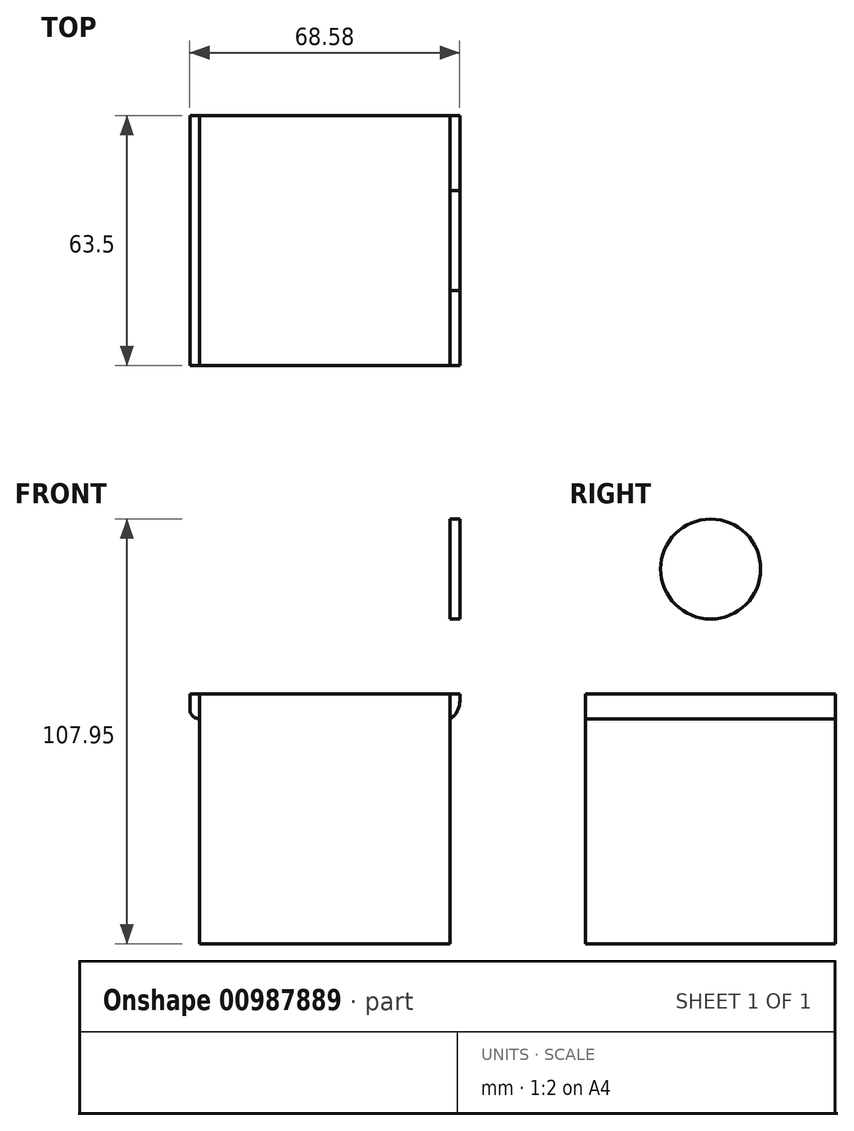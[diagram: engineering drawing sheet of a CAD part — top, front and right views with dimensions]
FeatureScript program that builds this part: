
annotation { "Feature Type Name" : "Feature", "Feature Type Description" : "" }
export const myFeature = defineFeature(function(context is Context, id is Id, definition is map)
    precondition{}
    {
        {
            var Q0;
            Q0=qCreatedBy(makeId("Top.planeOp"),FACE);
            var sketch = newSketch(context, id + "F0", { "sketchPlane" : qUnion([Q0])});
            skLineSegment(sketch, "E0.bottom", {"start": v(-78.16, 69.86) * mm, "end": v(-14.66, 69.86) * mm});
            skLineSegment(sketch, "E0.top", {"start": v(-78.16, 6.36) * mm, "end": v(-14.66, 6.36) * mm});
            skLineSegment(sketch, "E0.left", {"start": v(-78.16, 69.86) * mm, "end": v(-78.16, 6.36) * mm});
            skLineSegment(sketch, "E0.right", {"start": v(-14.66, 69.86) * mm, "end": v(-14.66, 6.36) * mm});
            skSolve(sketch);
        }
        {
            var Q0;
            Q0=makeQuery(id+"F0.imprint","IMPRINT",FACE,{"disambiguationData":[TD([[makeQuery(id+"F0.imprint","IMPRINT",EDGE,{"derivedFrom":sQuery(id+"F0.wireOp",EDGE,"E0.bottom")}),-1.0]])]});
            extrude(context, id + "F1", {"entities" : qUnion([Q0]), "depth" : 127 * mm, "offsetDistance" : 25.4 * mm});
        }
        {
            var Q0;
            Q0=makeQuery(id+"F1.opExtrude","SWEPT_FACE",FACE,{"disambiguationData":[OSD([sQuery(id+"F0.wireOp",EDGE,"E0.bottom")])]});
            var sketch = newSketch(context, id + "F2", { "sketchPlane" : qUnion([Q0])});
            skLineSegment(sketch, "E1.bottom", {"start": v(14.66, 127) * mm, "end": v(78.16, 127) * mm});
            skLineSegment(sketch, "E1.top", {"start": v(14.66, 63.5) * mm, "end": v(78.16, 63.5) * mm});
            skLineSegment(sketch, "E1.left", {"start": v(14.66, 127) * mm, "end": v(14.66, 63.5) * mm});
            skLineSegment(sketch, "E1.right", {"start": v(78.16, 127) * mm, "end": v(78.16, 63.5) * mm});
            skSolve(sketch);
        }
        {
            var Q0;
            Q0=makeQuery(id+"F2.imprint","IMPRINT",FACE,{"disambiguationData":[TD([[makeQuery(id+"F2.imprint","IMPRINT",EDGE,{"derivedFrom":sQuery(id+"F2.wireOp",EDGE,"E1.bottom")}),1.0]])]});
            extrude(context, id + "F3", {"entities" : qUnion([Q0]), "operationType" : NewBodyOperationType.ADD, "depth" : 2.54 * mm, "offsetDistance" : 25.4 * mm});
        }
        {
            var Q0;
            Q0=makeQuery(id+"F3.boolean.opBoolean","MERGE",FACE,{"derivedFrom":[makeQuery(id+"F1.opExtrude","SWEPT_FACE",FACE,{"disambiguationData":[OSD([sQuery(id+"F0.wireOp",EDGE,"E0.left")])]}),makeQuery(id+"F3.opExtrude","SWEPT_FACE",FACE,{"disambiguationData":[OSD([sQuery(id+"F2.wireOp",EDGE,"E1.right")])]})]});
            var sketch = newSketch(context, id + "F4", { "sketchPlane" : qUnion([Q0])});
            skLineSegment(sketch, "E2.bottom", {"start": v(-72.4, 127) * mm, "end": v(10.97, 127) * mm});
            skLineSegment(sketch, "E2.top", {"start": v(-72.4, 63.5) * mm, "end": v(10.97, 63.5) * mm});
            skLineSegment(sketch, "E2.left", {"start": v(-72.4, 127) * mm, "end": v(-72.4, 63.5) * mm});
            skLineSegment(sketch, "E2.right", {"start": v(10.97, 127) * mm, "end": v(10.97, 63.5) * mm});
            skSolve(sketch);
        }
        {
            var Q0;
            {var subQ0=sQuery(id+"F4.wireOp",EDGE,"E2.left");Q0=makeQuery(id+"F4.imprint","IMPRINT",FACE,{"disambiguationData":[TD([[makeQuery(id+"F4.imprint","IMPRINT",EDGE,{"derivedFrom":subQ0}),1.0]])]});}
            extrude(context, id + "F5", {"entities" : qUnion([Q0]), "operationType" : NewBodyOperationType.ADD, "depth" : 2.54 * mm, "offsetDistance" : 25.4 * mm});
        }
        {
            var Q0;
            Q0=makeQuery(id+"F3.boolean.opBoolean","MERGE",FACE,{"derivedFrom":[makeQuery(id+"F1.opExtrude","SWEPT_FACE",FACE,{"disambiguationData":[OSD([sQuery(id+"F0.wireOp",EDGE,"E0.right")])]}),makeQuery(id+"F3.opExtrude","SWEPT_FACE",FACE,{"disambiguationData":[OSD([sQuery(id+"F2.wireOp",EDGE,"E1.left")])]})]});
            var sketch = newSketch(context, id + "F6", { "sketchPlane" : qUnion([Q0])});
            skLineSegment(sketch, "E3.bottom", {"start": v(6.36, 127) * mm, "end": v(72.4, 127) * mm});
            skLineSegment(sketch, "E3.top", {"start": v(6.36, 63.5) * mm, "end": v(72.4, 63.5) * mm});
            skLineSegment(sketch, "E3.left", {"start": v(6.36, 127) * mm, "end": v(6.36, 63.5) * mm});
            skLineSegment(sketch, "E3.right", {"start": v(72.4, 127) * mm, "end": v(72.4, 63.5) * mm});
            skSolve(sketch);
        }
        {
            var Q0;
            Q0=makeQuery(id+"F6.imprint","IMPRINT",FACE,{"disambiguationData":[TD([[makeQuery(id+"F6.imprint","IMPRINT",EDGE,{"derivedFrom":sQuery(id+"F6.wireOp",EDGE,"E3.bottom")}),1.0]])]});
            extrude(context, id + "F7", {"entities" : qUnion([Q0]), "operationType" : NewBodyOperationType.ADD, "depth" : 2.54 * mm, "offsetDistance" : 25.4 * mm});
        }
        {
            var Q0;
            Q0=makeQuery(id+"F7.boolean.opBoolean","MERGE",FACE,{"derivedFrom":[makeQuery(id+"F5.boolean.opBoolean","MERGE",FACE,{"derivedFrom":[makeQuery(id+"F3.opExtrude","CAP_FACE",FACE,{"disambiguationData":[OSD([sQuery(id+"F2.wireOp",EDGE,"E1.bottom"),sQuery(id+"F2.wireOp",EDGE,"E1.top"),sQuery(id+"F2.wireOp",EDGE,"E1.left"),sQuery(id+"F2.wireOp",EDGE,"E1.right")])],"isStart":false}),makeQuery(id+"F5.opExtrude","SWEPT_FACE",FACE,{"disambiguationData":[OSD([sQuery(id+"F4.wireOp",EDGE,"E2.left")])]})]}),makeQuery(id+"F7.opExtrude","SWEPT_FACE",FACE,{"disambiguationData":[OSD([sQuery(id+"F6.wireOp",EDGE,"E3.right")])]})]});
            var sketch = newSketch(context, id + "F8", { "sketchPlane" : qUnion([Q0])});
            skLineSegment(sketch, "E4.bottom", {"start": v(12.12, 127) * mm, "end": v(80.7, 127) * mm});
            skLineSegment(sketch, "E4.top", {"start": v(12.12, 63.5) * mm, "end": v(80.7, 63.5) * mm});
            skLineSegment(sketch, "E4.left", {"start": v(12.12, 127) * mm, "end": v(12.12, 63.5) * mm});
            skLineSegment(sketch, "E4.right", {"start": v(80.7, 127) * mm, "end": v(80.7, 63.5) * mm});
            skSolve(sketch);
        }
        {
            var Q0;
            Q0=makeQuery(id+"F8.imprint","IMPRINT",FACE,{"disambiguationData":[TD([[makeQuery(id+"F8.imprint","IMPRINT",EDGE,{"derivedFrom":sQuery(id+"F8.wireOp",EDGE,"E4.bottom")}),1.0]])]});
            extrude(context, id + "F9", {"entities" : qUnion([Q0]), "operationType" : NewBodyOperationType.REMOVE, "oppositeDirection" : true, "depth" : 2.54 * mm, "offsetDistance" : 25.4 * mm});
        }
        {
            var Q0;
            {var subQ0=sQuery(id+"F0.wireOp",EDGE,"E0.top");Q0=makeQuery(id+"F7.boolean.opBoolean","MERGE",FACE,{"derivedFrom":[makeQuery(id+"F5.boolean.opBoolean","MERGE",FACE,{"derivedFrom":[makeQuery(id+"F1.opExtrude","SWEPT_FACE",FACE,{"disambiguationData":[OSD([subQ0])]}),makeQuery(id+"F5.opExtrude","SWEPT_FACE",FACE,{"disambiguationData":[OSD([subQ0,sQuery(id+"F0.wireOp",EDGE,"E0.left")])]})]}),makeQuery(id+"F7.opExtrude","SWEPT_FACE",FACE,{"disambiguationData":[OSD([sQuery(id+"F6.wireOp",EDGE,"E3.left")])]})]});}
            var sketch = newSketch(context, id + "F10", { "sketchPlane" : qUnion([Q0])});
            skLineSegment(sketch, "E5.bottom", {"start": v(-80.7, 127) * mm, "end": v(-12.12, 127) * mm});
            skLineSegment(sketch, "E5.top", {"start": v(-80.7, 63.5) * mm, "end": v(-12.12, 63.5) * mm});
            skLineSegment(sketch, "E5.left", {"start": v(-80.7, 127) * mm, "end": v(-80.7, 63.5) * mm});
            skLineSegment(sketch, "E5.right", {"start": v(-12.12, 127) * mm, "end": v(-12.12, 63.5) * mm});
            skLineSegment(sketch, "E6", {"start": v(-80.7, 127) * mm, "end": v(-78.16, 127) * mm});
            skLineSegment(sketch, "E7", {"start": v(-78.16, 127) * mm, "end": v(-14.66, 127) * mm});
            skLineSegment(sketch, "E8", {"start": v(-14.66, 127) * mm, "end": v(-12.12, 127) * mm});
            skLineSegment(sketch, "E9.top", {"start": v(-78.16, 63.5) * mm, "end": v(-14.66, 63.5) * mm});
            skLineSegment(sketch, "E9.left", {"start": v(-78.16, 127) * mm, "end": v(-78.16, 63.5) * mm});
            skLineSegment(sketch, "E9.right", {"start": v(-14.66, 127) * mm, "end": v(-14.66, 63.5) * mm});
            skSolve(sketch);
        }
        {
            var Q0;
            {var subQ0=sQuery(id+"F10.wireOp",EDGE,"E9.left");Q0=makeQuery(id+"F10.imprint","IMPRINT",FACE,{"disambiguationData":[TD([[makeQuery(id+"F10.imprint","IMPRINT",EDGE,{"derivedFrom":subQ0}),1.0]])]});}
            extrude(context, id + "F11", {"entities" : qUnion([Q0]), "operationType" : NewBodyOperationType.REMOVE, "endBound" : BoundingType.THROUGH_ALL, "oppositeDirection" : true, "depth" : 25.4 * mm, "offsetDistance" : 25.4 * mm});
        }
        {
            var Q0;
            {var subQ0=sQuery(id+"F0.wireOp",EDGE,"E0.left");var subQ2=sQuery(id+"F4.wireOp",EDGE,"E2.top");Q0=makeQuery(id+"F9.boolean.opBoolean","SPLIT",FACE,{"disambiguationData":[TD([makeQuery(id+"F1.opExtrude","SWEPT_FACE",FACE,{"disambiguationData":[OSD([subQ0])]})])],"derivedFrom":makeQuery(id+"F7.boolean.opBoolean","MERGE",FACE,{"derivedFrom":[makeQuery(id+"F5.boolean.opBoolean","MERGE",FACE,{"derivedFrom":[makeQuery(id+"F3.opExtrude","SWEPT_FACE",FACE,{"disambiguationData":[OSD([sQuery(id+"F2.wireOp",EDGE,"E1.top")])]}),makeQuery(id+"F5.opExtrude","SWEPT_FACE",FACE,{"disambiguationData":[OSD([subQ2])]})]}),makeQuery(id+"F7.opExtrude","SWEPT_FACE",FACE,{"disambiguationData":[OSD([sQuery(id+"F6.wireOp",EDGE,"E3.top")])]})]})});}
            var Q1;
            {var subQ2=sQuery(id+"F6.wireOp",EDGE,"E3.top");Q1=makeQuery(id+"F9.boolean.opBoolean","SPLIT",FACE,{"disambiguationData":[TD([makeQuery(id+"F1.opExtrude","SWEPT_FACE",FACE,{"disambiguationData":[OSD([sQuery(id+"F0.wireOp",EDGE,"E0.right")])]})])],"derivedFrom":makeQuery(id+"F7.boolean.opBoolean","MERGE",FACE,{"derivedFrom":[makeQuery(id+"F5.boolean.opBoolean","MERGE",FACE,{"derivedFrom":[makeQuery(id+"F3.opExtrude","SWEPT_FACE",FACE,{"disambiguationData":[OSD([sQuery(id+"F2.wireOp",EDGE,"E1.top")])]}),makeQuery(id+"F5.opExtrude","SWEPT_FACE",FACE,{"disambiguationData":[OSD([sQuery(id+"F4.wireOp",EDGE,"E2.top")])]})]}),makeQuery(id+"F7.opExtrude","SWEPT_FACE",FACE,{"disambiguationData":[OSD([subQ2])]})]})});}
            extrude(context, id + "F12", {"entities" : qUnion([Q0, Q1]), "depth" : 6.35 * mm, "offsetDistance" : 25.4 * mm});
        }
        {
            var Q0;
            Q0=makeQuery(id+"F12.opExtrude","CAP_EDGE",EDGE,{"disambiguationData":[OSD([sQuery(id+"F4.wireOp",EDGE,"E2.top")])],"isStart":false});
            fillet(context, id + "F13", {"entities" : qUnion([Q0]), "radius" : 2.54 * mm, "tangentPropagation" : true, "allowEdgeOverflow" : false});
        }
        {
            var Q0;
            Q0=makeQuery(id+"F12.opExtrude","CAP_EDGE",EDGE,{"disambiguationData":[OSD([sQuery(id+"F6.wireOp",EDGE,"E3.top")])],"isStart":false});
            fillet(context, id + "F14", {"entities" : qUnion([Q0]), "radius" : 5.08 * mm, "tangentPropagation" : true, "allowEdgeOverflow" : false});
        }
        {
            var Q0;
            Q0=makeQuery(id+"F7.opExtrude","CAP_FACE",FACE,{"disambiguationData":[OSD([sQuery(id+"F6.wireOp",EDGE,"E3.bottom"),sQuery(id+"F6.wireOp",EDGE,"E3.top"),sQuery(id+"F6.wireOp",EDGE,"E3.left"),sQuery(id+"F6.wireOp",EDGE,"E3.right")])],"isStart":false});
            var sketch = newSketch(context, id + "F15", { "sketchPlane" : qUnion([Q0])});
            skLineSegment(sketch, "E10", {"start": v(6.36, 127) * mm, "end": v(69.86, 127) * mm});
            skLineSegment(sketch, "E11", {"start": v(69.86, 127) * mm, "end": v(38.11, 127) * mm});
            skLineSegment(sketch, "E12", {"start": v(38.11, 127) * mm, "end": v(38.11, 63.5) * mm});
            skLineSegment(sketch, "E13", {"start": v(38.11, 63.5) * mm, "end": v(38.11, 95.25) * mm});
            skCircle(sketch, "E14", {"center": v(38.11, 95.25) * mm, "radius": 12.7 * mm});
            skSolve(sketch);
        }
        {
            var Q0;
            {var subQ0=sQuery(id+"F15.wireOp",EDGE,"E13");var subQ1=sQuery(id+"F15.wireOp",EDGE,"E12");var subQ2=makeQuery(id+"F15.imprint","INTERSECT",VERTEX,{"derivedFrom":[subQ1,subQ0]});Q0=makeQuery(id+"F15.imprint","IMPRINT",FACE,{"disambiguationData":[TD([[makeQuery(id+"F15.imprint","IMPRINT",EDGE,{"disambiguationData":[TD([[subQ2,1.0]])],"derivedFrom":subQ1}),-1.0]])]});}
            var Q1;
            {var subQ0=sQuery(id+"F15.wireOp",EDGE,"E13");var subQ1=sQuery(id+"F15.wireOp",EDGE,"E12");var subQ2=makeQuery(id+"F15.imprint","INTERSECT",VERTEX,{"derivedFrom":[subQ1,subQ0]});Q1=makeQuery(id+"F15.imprint","IMPRINT",FACE,{"disambiguationData":[TD([[makeQuery(id+"F15.imprint","IMPRINT",EDGE,{"disambiguationData":[TD([[subQ2,1.0]])],"derivedFrom":subQ1}),1.0]])]});}
            extrude(context, id + "F16", {"entities" : qUnion([Q0, Q1]), "operationType" : NewBodyOperationType.REMOVE, "oppositeDirection" : true, "depth" : 127 * mm, "offsetDistance" : 25.4 * mm});
        }
        {
            var Q0;
            Q0=makeQuery(id+"F5.opExtrude","CAP_FACE",FACE,{"disambiguationData":[OSD([sQuery(id+"F0.wireOp",EDGE,"E0.top"),sQuery(id+"F0.wireOp",EDGE,"E0.left"),sQuery(id+"F4.wireOp",EDGE,"E2.bottom"),sQuery(id+"F4.wireOp",EDGE,"E2.top"),sQuery(id+"F4.wireOp",EDGE,"E2.left")])],"isStart":false});
            var sketch = newSketch(context, id + "F17", { "sketchPlane" : qUnion([Q0])});
            skLineSegment(sketch, "E15", {"start": v(-69.86, 127) * mm, "end": v(-38.11, 127) * mm});
            skLineSegment(sketch, "E16", {"start": v(-38.11, 127) * mm, "end": v(-38.11, 63.5) * mm});
            skLineSegment(sketch, "E17", {"start": v(-38.11, 63.5) * mm, "end": v(-38.11, 95.25) * mm});
            skLineSegment(sketch, "E18", {"start": v(-38.11, 95.25) * mm, "end": v(-69.86, 95.25) * mm});
            skCircle(sketch, "E19", {"center": v(-38.11, 95.25) * mm, "radius": 12.7 * mm});
            skSolve(sketch);
        }
        {
            var Q0;
            {var subQ1=sQuery(id+"F17.wireOp",EDGE,"E16");var subQ3=sQuery(id+"F17.wireOp",EDGE,"E19");var subQ4=makeQuery(id+"F17.imprint","INTERSECT",VERTEX,{"derivedFrom":[subQ1,subQ3]});Q0=makeQuery(id+"F17.imprint","IMPRINT",FACE,{"disambiguationData":[TD([[makeQuery(id+"F17.imprint","IMPRINT",EDGE,{"disambiguationData":[TD([[subQ4,-1.0]])],"derivedFrom":subQ3}),1.0]])]});}
            var Q1;
            {var subQ1=sQuery(id+"F17.wireOp",EDGE,"E17");var subQ3=sQuery(id+"F17.wireOp",EDGE,"E19");var subQ4=makeQuery(id+"F17.imprint","INTERSECT",VERTEX,{"derivedFrom":[subQ1,subQ3]});Q1=makeQuery(id+"F17.imprint","IMPRINT",FACE,{"disambiguationData":[TD([[makeQuery(id+"F17.imprint","IMPRINT",EDGE,{"disambiguationData":[TD([[subQ4,1.0]])],"derivedFrom":subQ3}),1.0]])]});}
            var Q2;
            {var subQ1=sQuery(id+"F17.wireOp",EDGE,"E16");var subQ3=sQuery(id+"F17.wireOp",EDGE,"E19");var subQ4=makeQuery(id+"F17.imprint","INTERSECT",VERTEX,{"derivedFrom":[subQ1,subQ3]});Q2=makeQuery(id+"F17.imprint","IMPRINT",FACE,{"disambiguationData":[TD([[makeQuery(id+"F17.imprint","IMPRINT",EDGE,{"disambiguationData":[TD([[subQ4,1.0]])],"derivedFrom":subQ3}),1.0]])]});}
            extrude(context, id + "F18", {"entities" : qUnion([Q0, Q1, Q2]), "operationType" : NewBodyOperationType.REMOVE, "oppositeDirection" : true, "depth" : 25.4 * mm, "offsetDistance" : 25.4 * mm});
        }
    });
